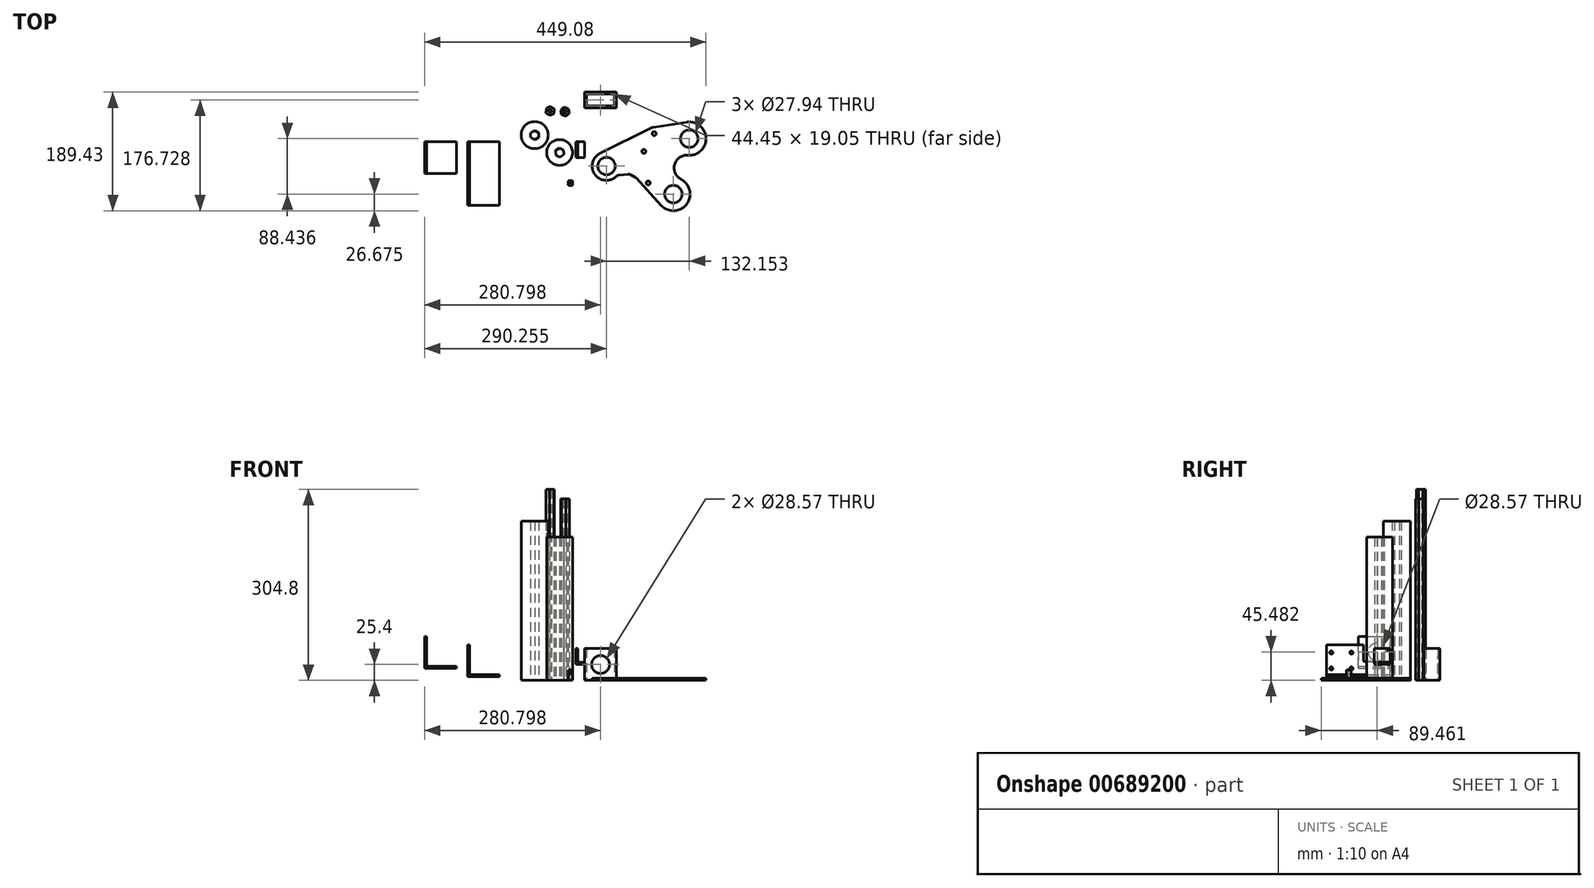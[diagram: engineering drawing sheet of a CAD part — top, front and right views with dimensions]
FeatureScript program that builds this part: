
annotation { "Feature Type Name" : "Feature", "Feature Type Description" : "" }
export const myFeature = defineFeature(function(context is Context, id is Id, definition is map)
    precondition{}
    {
        {
            var Q0;
            Q0=qCreatedBy(makeId("Top.planeOp"),FACE);
            var sketch = newSketch(context, id + "F0", { "sketchPlane" : qUnion([Q0])});
            skCircle(sketch, "E0", {"center": v(-44.27, 47.98) * mm, "radius": 2.55 * mm});
            skCircle(sketch, "E1.cCircle", {"center": v(-44.27, 47.98) * mm, "radius": 6.35 * mm, "construction": true});
            skLineSegment(sketch, "E1.0", {"start": v(-42.75, 40.8) * mm, "end": v(-49.72, 43.08) * mm});
            skLineSegment(sketch, "E1.1", {"start": v(-49.72, 43.08) * mm, "end": v(-51.24, 50.25) * mm});
            skLineSegment(sketch, "E1.2", {"start": v(-51.24, 50.25) * mm, "end": v(-45.79, 55.15) * mm});
            skLineSegment(sketch, "E1.3", {"start": v(-45.79, 55.15) * mm, "end": v(-38.82, 52.88) * mm});
            skLineSegment(sketch, "E1.4", {"start": v(-38.82, 52.88) * mm, "end": v(-37.3, 45.71) * mm});
            skLineSegment(sketch, "E1.5", {"start": v(-37.3, 45.71) * mm, "end": v(-42.75, 40.8) * mm});
            skPoint(sketch, "E1.0.midPoint", {"position": v(-46.23, 41.94) * mm});
            skCircle(sketch, "E2", {"center": v(-68.05, 49.07) * mm, "radius": 2.55 * mm});
            skCircle(sketch, "E3.cCircle", {"center": v(-68.05, 49.07) * mm, "radius": 6.35 * mm, "construction": true});
            skLineSegment(sketch, "E3.0", {"start": v(-62.1, 44.78) * mm, "end": v(-68.8, 41.78) * mm});
            skLineSegment(sketch, "E3.1", {"start": v(-68.8, 41.78) * mm, "end": v(-74.74, 46.07) * mm});
            skLineSegment(sketch, "E3.2", {"start": v(-74.74, 46.07) * mm, "end": v(-74, 53.36) * mm});
            skLineSegment(sketch, "E3.3", {"start": v(-74, 53.36) * mm, "end": v(-67.31, 56.37) * mm});
            skLineSegment(sketch, "E3.4", {"start": v(-67.31, 56.37) * mm, "end": v(-61.36, 52.08) * mm});
            skLineSegment(sketch, "E3.5", {"start": v(-61.36, 52.08) * mm, "end": v(-62.1, 44.78) * mm});
            skPoint(sketch, "E3.0.midPoint", {"position": v(-65.45, 43.28) * mm});
            skSolve(sketch);
        }
        {
            var Q0;
            Q0=makeQuery(id+"F0.imprint","IMPRINT",FACE,{"disambiguationData":[TD([[makeQuery(id+"F0.imprint","IMPRINT",EDGE,{"derivedFrom":sQuery(id+"F0.wireOp",EDGE,"E0")}),-1.0]])]});
            extrude(context, id + "F1", {"entities" : qUnion([Q0]), "depth" : 289.56 * mm, "offsetDistance" : 25.4 * mm});
        }
        {
            var Q0;
            Q0=makeQuery(id+"F0.imprint","IMPRINT",FACE,{"disambiguationData":[TD([[makeQuery(id+"F0.imprint","IMPRINT",EDGE,{"derivedFrom":sQuery(id+"F0.wireOp",EDGE,"E2")}),-1.0]])]});
            extrude(context, id + "F2", {"entities" : qUnion([Q0]), "depth" : 304.8 * mm, "offsetDistance" : 25.4 * mm});
        }
        {
            var Q0;
            Q0=qCreatedBy(makeId("Top.planeOp"),FACE);
            var sketch = newSketch(context, id + "F3", { "sketchPlane" : qUnion([Q0])});
            skCircle(sketch, "E4", {"center": v(128.7, -83.53) * mm, "radius": 13.97 * mm});
            skArc(sketch, "E5", {"start": v(150.08, -21.45) * mm, "mid": v(130.5, -37.06) * mm, "end": v(140.94, -59.83) * mm});
            skCircle(sketch, "E6", {"center": v(154.1, 4.91) * mm, "radius": 13.97 * mm});
            skCircle(sketch, "E7", {"center": v(154.1, 4.91) * mm, "radius": 20.64 * mm, "construction": true});
            skCircle(sketch, "E8", {"center": v(128.7, -83.53) * mm, "radius": 21.59 * mm, "construction": true});
            skArc(sketch, "E9", {"start": v(108.94, -101.43) * mm, "mid": v(132.45, -109.93) * mm, "end": v(152.67, -95.23) * mm});
            skLineSegment(sketch, "E10", {"start": v(150.12, 31.28) * mm, "end": v(96.62, 23.19) * mm});
            skLineSegment(sketch, "E11.bottom", {"start": v(224.17, -25.6) * mm, "end": v(499.33, -74.11) * mm, "construction": true});
            skLineSegment(sketch, "E11.top", {"start": v(215.35, -75.62) * mm, "end": v(490.5, -124.14) * mm, "construction": true});
            skLineSegment(sketch, "E11.left", {"start": v(224.17, -25.6) * mm, "end": v(215.35, -75.62) * mm, "construction": true});
            skLineSegment(sketch, "E11.right", {"start": v(499.33, -74.11) * mm, "end": v(490.5, -124.14) * mm, "construction": true});
            skPoint(sketch, "E11.middle", {"position": v(357.34, -74.87) * mm});
            skCircle(sketch, "E12", {"center": v(81.54, -15.44) * mm, "radius": 3.18 * mm});
            skCircle(sketch, "E13", {"center": v(81.54, -15.44) * mm, "radius": 6.87 * mm, "construction": true});
            skArc(sketch, "E14", {"start": v(11.8, -18.31) * mm, "mid": v(4, -52.95) * mm, "end": v(39.5, -53.45) * mm});
            skCircle(sketch, "E15", {"center": v(21.96, -38.8) * mm, "radius": 13.97 * mm});
            skArc(sketch, "E16.trimOffspring", {"start": v(152.67, -95.23) * mm, "mid": v(154.03, -75.14) * mm, "end": v(140.94, -59.83) * mm});
            skLineSegment(sketch, "E17", {"start": v(58.9, -51.49) * mm, "end": v(69.35, -57.7) * mm});
            skLineSegment(sketch, "E18", {"start": v(39.5, -53.45) * mm, "end": v(58.9, -51.49) * mm});
            skCircle(sketch, "E19", {"center": v(98.16, 13.02) * mm, "radius": 3.18 * mm});
            skCircle(sketch, "E20", {"center": v(98.16, 13.02) * mm, "radius": 6.87 * mm, "construction": true});
            skLineSegment(sketch, "E21", {"start": v(154.1, 4.91) * mm, "end": v(21.96, -38.8) * mm, "construction": true});
            skArc(sketch, "E22", {"start": v(96.62, 23.19) * mm, "mid": v(95.07, 22.83) * mm, "end": v(93.59, 22.23) * mm});
            skArc(sketch, "E23.trimOffspring", {"start": v(150.08, -21.45) * mm, "mid": v(180.78, 4.9) * mm, "end": v(150.12, 31.28) * mm});
            skLineSegment(sketch, "E24", {"start": v(69.35, -57.7) * mm, "end": v(108.94, -101.43) * mm});
            skArc(sketch, "E25.0.startCap", {"start": v(148.5, 21.86) * mm, "mid": v(171.06, 10.52) * mm, "end": v(159.71, -12.04) * mm, "construction": true});
            skArc(sketch, "E25.0.endCap", {"start": v(27.56, -55.75) * mm, "mid": v(5, -44.4) * mm, "end": v(16.35, -21.84) * mm, "construction": true});
            skLineSegment(sketch, "E25.0.left", {"start": v(159.71, -12.04) * mm, "end": v(27.56, -55.75) * mm, "construction": true});
            skLineSegment(sketch, "E25.0.right", {"start": v(148.5, 21.86) * mm, "end": v(16.35, -21.84) * mm, "construction": true});
            skCircle(sketch, "E26", {"center": v(88.6, -65.7) * mm, "radius": 3.18 * mm});
            skCircle(sketch, "E27", {"center": v(88.6, -65.7) * mm, "radius": 6.87 * mm, "construction": true});
            skLineSegment(sketch, "E28", {"start": v(81.54, -15.44) * mm, "end": v(88.5, -65) * mm, "construction": true});
            skLineSegment(sketch, "E29", {"start": v(93.59, 22.23) * mm, "end": v(11.8, -18.31) * mm});
            skSolve(sketch);
        }
        {
            var Q0;
            Q0=makeQuery(id+"F3.imprint","IMPRINT",FACE,{"disambiguationData":[TD([[makeQuery(id+"F3.imprint","IMPRINT",EDGE,{"derivedFrom":sQuery(id+"F3.wireOp",EDGE,"E4")}),-1.0]])]});
            var Q1;
            Q1=makeQuery(id+"F3.imprint","IMPRINT",FACE,{"disambiguationData":[TD([[makeQuery(id+"F3.imprint","IMPRINT",EDGE,{"derivedFrom":sQuery(id+"F3.wireOp",EDGE,"E15")}),-1.0]])]});
            var Q2;
            Q2=makeQuery(id+"F3.imprint","IMPRINT",FACE,{"disambiguationData":[TD([[makeQuery(id+"F3.imprint","IMPRINT",EDGE,{"derivedFrom":sQuery(id+"F3.wireOp",EDGE,"E6")}),-1.0]])]});
            var Q3;
            Q3=makeQuery(id+"F3.imprint","IMPRINT",FACE,{"disambiguationData":[TD([[makeQuery(id+"F3.imprint","IMPRINT",EDGE,{"derivedFrom":sQuery(id+"F3.wireOp",EDGE,"E19")}),-1.0]])]});
            extrude(context, id + "F4", {"entities" : qUnion([Q0, Q1, Q2, Q3]), "depth" : 3.17 * mm, "offsetDistance" : 25.4 * mm});
        }
        {
            var Q0;
            Q0=qCreatedBy(makeId("Top.planeOp"),FACE);
            var sketch = newSketch(context, id + "F5", { "sketchPlane" : qUnion([Q0])});
            skCircle(sketch, "E30", {"center": v(-92.7, 10.62) * mm, "radius": 21.59 * mm});
            skCircle(sketch, "E31.cCircle", {"center": v(-92.7, 10.62) * mm, "radius": 6.35 * mm, "construction": true});
            skLineSegment(sketch, "E31.0", {"start": v(-86.35, 6.96) * mm, "end": v(-92.7, 3.29) * mm});
            skLineSegment(sketch, "E31.1", {"start": v(-92.7, 3.29) * mm, "end": v(-99.05, 6.95) * mm});
            skLineSegment(sketch, "E31.2", {"start": v(-99.05, 6.95) * mm, "end": v(-99.06, 14.28) * mm});
            skLineSegment(sketch, "E31.3", {"start": v(-99.06, 14.28) * mm, "end": v(-92.7, 17.95) * mm});
            skLineSegment(sketch, "E31.4", {"start": v(-92.7, 17.95) * mm, "end": v(-86.36, 14.29) * mm});
            skLineSegment(sketch, "E31.5", {"start": v(-86.36, 14.29) * mm, "end": v(-86.35, 6.96) * mm});
            skPoint(sketch, "E31.0.midPoint", {"position": v(-89.53, 5.12) * mm});
            skSolve(sketch);
        }
        {
            var Q0;
            Q0=qSketchRegion(id+"F5",true);
            extrude(context, id + "F6", {"entities" : qUnion([Q0]), "depth" : 254 * mm, "offsetDistance" : 25.4 * mm});
        }
        {
            var Q0;
            Q0=qCreatedBy(makeId("Top.planeOp"),FACE);
            var sketch = newSketch(context, id + "F7", { "sketchPlane" : qUnion([Q0])});
            skCircle(sketch, "E32", {"center": v(-52.83, -17.18) * mm, "radius": 20.64 * mm});
            skCircle(sketch, "E33.cCircle", {"center": v(-52.83, -17.18) * mm, "radius": 6.35 * mm, "construction": true});
            skLineSegment(sketch, "E33.0", {"start": v(-46.29, -20.49) * mm, "end": v(-52.42, -24.5) * mm});
            skLineSegment(sketch, "E33.1", {"start": v(-52.42, -24.5) * mm, "end": v(-58.97, -21.2) * mm});
            skLineSegment(sketch, "E33.2", {"start": v(-58.97, -21.2) * mm, "end": v(-59.38, -13.88) * mm});
            skLineSegment(sketch, "E33.3", {"start": v(-59.38, -13.88) * mm, "end": v(-53.25, -9.86) * mm});
            skLineSegment(sketch, "E33.4", {"start": v(-53.25, -9.86) * mm, "end": v(-46.7, -13.17) * mm});
            skLineSegment(sketch, "E33.5", {"start": v(-46.7, -13.17) * mm, "end": v(-46.29, -20.49) * mm});
            skPoint(sketch, "E33.0.midPoint", {"position": v(-49.35, -22.5) * mm});
            skSolve(sketch);
        }
        {
            var Q0;
            Q0=makeQuery(id+"F7.imprint","IMPRINT",FACE,{"disambiguationData":[TD([[makeQuery(id+"F7.imprint","IMPRINT",EDGE,{"derivedFrom":sQuery(id+"F7.wireOp",EDGE,"E32")}),1.0]])]});
            extrude(context, id + "F8", {"entities" : qUnion([Q0]), "depth" : 228.6 * mm, "offsetDistance" : 25.4 * mm});
        }
        {
            var Q0;
            Q0=makeQuery(id+"F4.opExtrude","SWEPT_EDGE",EDGE,{"disambiguationData":[OSD([sQuery(id+"F3.wireOp",EDGE,"E10"),sQuery(id+"F3.wireOp",EDGE,"zxEpT3On-8kar-o6cf-8kjg-F8as8R4mIhED")])]});
            var Q1;
            Q1=makeQuery(id+"F4.opExtrude","SWEPT_EDGE",EDGE,{"disambiguationData":[OSD([sQuery(id+"F3.wireOp",EDGE,"E9"),sQuery(id+"F3.wireOp",EDGE,"c811799d-0cea-4770-864e-a57e5c831115.trimOffspring")])]});
            var Q2;
            Q2=makeQuery(id+"F4.opExtrude","SWEPT_EDGE",EDGE,{"disambiguationData":[OSD([sQuery(id+"F3.wireOp",EDGE,"4rDKKqdp-8bAY-1tYy-HnWQ-ftVNqJqIiV7y"),sQuery(id+"F3.wireOp",EDGE,"c811799d-0cea-4770-864e-a57e5c831115.trimOffspring")])]});
            var Q3;
            Q3=makeQuery(id+"F4.opExtrude","SWEPT_EDGE",EDGE,{"disambiguationData":[OSD([sQuery(id+"F3.wireOp",EDGE,"4rDKKqdp-8bAY-1tYy-HnWQ-ftVNqJqIiV7y"),sQuery(id+"F3.wireOp",EDGE,"E17")])]});
            var Q4;
            Q4=makeQuery(id+"F4.opExtrude","SWEPT_EDGE",EDGE,{"disambiguationData":[OSD([sQuery(id+"F3.wireOp",EDGE,"E14"),sQuery(id+"F3.wireOp",EDGE,"E18")])]});
            var Q5;
            Q5=makeQuery(id+"F4.opExtrude","SWEPT_EDGE",EDGE,{"disambiguationData":[OSD([sQuery(id+"F3.wireOp",EDGE,"E17"),sQuery(id+"F3.wireOp",EDGE,"E18")])]});
            var Q6;
            Q6=makeQuery(id+"F4.opExtrude","SWEPT_EDGE",EDGE,{"disambiguationData":[OSD([sQuery(id+"F3.wireOp",EDGE,"NqwyW4cG-bsPY-CdaV-dfMR-VU6UGlkVoTuP"),sQuery(id+"F3.wireOp",EDGE,"JTzklvK0-043S-AxbH-GuJj-bxXyPtfSXbyR")])]});
            fillet(context, id + "F9", {"entities" : qUnion([Q0, Q1, Q2, Q3, Q4, Q5, Q6]), "radius" : 6.35 * mm, "tangentPropagation" : true, "allowEdgeOverflow" : false});
        }
        {
            var Q0;
            Q0=qCreatedBy(makeId("Top.planeOp"),FACE);
            var sketch = newSketch(context, id + "F10", { "sketchPlane" : qUnion([Q0])});
            skLineSegment(sketch, "E34.bottom", {"start": v(37.9, 79.23) * mm, "end": v(-12.9, 79.23) * mm});
            skLineSegment(sketch, "E34.top", {"start": v(37.9, 53.83) * mm, "end": v(-12.9, 53.83) * mm});
            skLineSegment(sketch, "E34.left", {"start": v(37.9, 79.23) * mm, "end": v(37.9, 53.83) * mm});
            skLineSegment(sketch, "E34.right", {"start": v(-12.9, 79.23) * mm, "end": v(-12.9, 53.83) * mm});
            skPoint(sketch, "E34.middle", {"position": v(12.5, 66.53) * mm});
            skLineSegment(sketch, "E35.bottom", {"start": v(34.72, 76.05) * mm, "end": v(-9.73, 76.05) * mm});
            skLineSegment(sketch, "E35.top", {"start": v(34.72, 57) * mm, "end": v(-9.73, 57) * mm});
            skLineSegment(sketch, "E35.left", {"start": v(34.72, 76.05) * mm, "end": v(34.72, 57) * mm});
            skLineSegment(sketch, "E35.right", {"start": v(-9.73, 76.05) * mm, "end": v(-9.73, 57) * mm});
            skSolve(sketch);
        }
        {
            var Q0;
            Q0=makeQuery(id+"F10.imprint","IMPRINT",FACE,{"disambiguationData":[TD([[makeQuery(id+"F10.imprint","IMPRINT",EDGE,{"derivedFrom":sQuery(id+"F10.wireOp",EDGE,"E34.bottom")}),1.0]])]});
            extrude(context, id + "F11", {"entities" : qUnion([Q0]), "depth" : 50.8 * mm, "offsetDistance" : 25.4 * mm});
        }
        {
            var Q0;
            Q0=makeQuery(id+"F11.opExtrude","SWEPT_FACE",FACE,{"disambiguationData":[OSD([sQuery(id+"F10.wireOp",EDGE,"E34.bottom")])]});
            var sketch = newSketch(context, id + "F12", { "sketchPlane" : qUnion([Q0])});
            skLineSegment(sketch, "E36.0.0", {"start": v(-37.9, 0) * mm, "end": v(12.9, 0) * mm, "construction": true});
            skLineSegment(sketch, "E36.0.1", {"start": v(12.9, 0) * mm, "end": v(12.9, 50.8) * mm, "construction": true});
            skLineSegment(sketch, "E36.0.2", {"start": v(12.9, 50.8) * mm, "end": v(-37.9, 50.8) * mm, "construction": true});
            skLineSegment(sketch, "E36.0.3", {"start": v(-37.9, 50.8) * mm, "end": v(-37.9, 0) * mm, "construction": true});
            skCircle(sketch, "E37", {"center": v(-12.5, 25.4) * mm, "radius": 14.29 * mm});
            skPoint(sketch, "E37.centerSnap0", {"position": v(-12.5, 50.8) * mm});
            skSolve(sketch);
        }
        {
            var Q0;
            Q0=makeQuery(id+"F12.imprint","IMPRINT",FACE,{"disambiguationData":[TD([[makeQuery(id+"F12.imprint","IMPRINT",EDGE,{"derivedFrom":sQuery(id+"F12.wireOp",EDGE,"E37")}),1.0]])]});
            var Q1;
            Q1=makeQuery(id+"F11.opExtrude","SWEPT_FACE",FACE,{"disambiguationData":[OSD([sQuery(id+"F10.wireOp",EDGE,"E34.top")])]});
            extrude(context, id + "F13", {"entities" : qUnion([Q0]), "operationType" : NewBodyOperationType.REMOVE, "endBound" : BoundingType.UP_TO_SURFACE, "oppositeDirection" : true, "depth" : 25.4 * mm, "endBoundEntityFace" : qUnion([Q1]), "offsetDistance" : 25.4 * mm});
        }
        {
            var Q0;
            Q0=qCreatedBy(makeId("Front.planeOp"),FACE);
            var sketch = newSketch(context, id + "F14", { "sketchPlane" : qUnion([Q0])});
            skLineSegment(sketch, "E38", {"start": v(-199.8, 56.53) * mm, "end": v(-199.8, 5.73) * mm});
            skLineSegment(sketch, "E39", {"start": v(-199.8, 5.73) * mm, "end": v(-149, 5.73) * mm});
            skLineSegment(sketch, "E40", {"start": v(-149, 5.73) * mm, "end": v(-149, 8.9) * mm});
            skLineSegment(sketch, "E41", {"start": v(-149, 8.9) * mm, "end": v(-196.63, 8.9) * mm});
            skLineSegment(sketch, "E42", {"start": v(-196.63, 8.9) * mm, "end": v(-196.63, 56.53) * mm});
            skLineSegment(sketch, "E43", {"start": v(-196.63, 56.53) * mm, "end": v(-199.8, 56.53) * mm});
            skSolve(sketch);
        }
        {
            var Q0;
            Q0=qSketchRegion(id+"F14",true);
            extrude(context, id + "F15", {"entities" : qUnion([Q0]), "depth" : 101.6 * mm, "offsetDistance" : 25.4 * mm});
        }
        {
            var Q0;
            Q0=makeQuery(id+"F15.opExtrude","SWEPT_FACE",FACE,{"disambiguationData":[OSD([sQuery(id+"F14.wireOp",EDGE,"E42")])]});
            var sketch = newSketch(context, id + "F16", { "sketchPlane" : qUnion([Q0])});
            skLineSegment(sketch, "E44.0.0", {"start": v(0, 8.9) * mm, "end": v(0, 56.53) * mm, "construction": true});
            skLineSegment(sketch, "E44.0.1", {"start": v(0, 56.53) * mm, "end": v(-101.6, 56.53) * mm, "construction": true});
            skLineSegment(sketch, "E44.0.2", {"start": v(-101.6, 56.53) * mm, "end": v(-101.6, 8.9) * mm, "construction": true});
            skLineSegment(sketch, "E44.0.3", {"start": v(-101.6, 8.9) * mm, "end": v(0, 8.9) * mm, "construction": true});
            skLineSegment(sketch, "E45.bottom", {"start": v(-93.98, 44.46) * mm, "end": v(-61.85, 44.46) * mm, "construction": true});
            skLineSegment(sketch, "E45.top", {"start": v(-93.98, 19.06) * mm, "end": v(-61.85, 19.06) * mm, "construction": true});
            skLineSegment(sketch, "E45.left", {"start": v(-93.98, 44.46) * mm, "end": v(-93.98, 19.06) * mm, "construction": true});
            skLineSegment(sketch, "E45.right", {"start": v(-61.85, 44.46) * mm, "end": v(-61.85, 19.06) * mm, "construction": true});
            skPoint(sketch, "E45.middle", {"position": v(-77.91, 31.76) * mm});
            skCircle(sketch, "E46", {"center": v(-93.98, 44.46) * mm, "radius": 2.55 * mm});
            skCircle(sketch, "E47", {"center": v(-93.98, 19.06) * mm, "radius": 2.55 * mm});
            skCircle(sketch, "E48", {"center": v(-61.85, 19.06) * mm, "radius": 2.55 * mm});
            skCircle(sketch, "E49", {"center": v(-61.85, 44.46) * mm, "radius": 2.55 * mm});
            skLineSegment(sketch, "E50", {"start": v(-42.78, 56.53) * mm, "end": v(-42.78, 29.99) * mm});
            skLineSegment(sketch, "E51", {"start": v(-42.78, 29.99) * mm, "end": v(0, 29.99) * mm});
            skLineSegment(sketch, "E52", {"start": v(0, 29.99) * mm, "end": v(0, 56.53) * mm});
            skLineSegment(sketch, "E53", {"start": v(-42.78, 56.53) * mm, "end": v(0, 56.53) * mm});
            skSolve(sketch);
        }
        {
            var Q0;
            Q0=qSketchRegion(id+"F16",true);
            var Q1;
            Q1=makeQuery(id+"F15.opExtrude","SWEPT_FACE",FACE,{"disambiguationData":[OSD([sQuery(id+"F14.wireOp",EDGE,"E38")])]});
            extrude(context, id + "F17", {"entities" : qUnion([Q0]), "operationType" : NewBodyOperationType.REMOVE, "endBound" : BoundingType.UP_TO_SURFACE, "oppositeDirection" : true, "depth" : 25.4 * mm, "endBoundEntityFace" : qUnion([Q1]), "offsetDistance" : 25.4 * mm});
        }
        {
            var Q0;
            Q0=qCreatedBy(makeId("Front.planeOp"),FACE);
            var sketch = newSketch(context, id + "F18", { "sketchPlane" : qUnion([Q0])});
            skLineSegment(sketch, "E54", {"start": v(-26.85, 51.37) * mm, "end": v(-26.85, 25.97) * mm});
            skLineSegment(sketch, "E55", {"start": v(-26.85, 25.97) * mm, "end": v(-12.88, 25.97) * mm});
            skLineSegment(sketch, "E56", {"start": v(-12.88, 25.97) * mm, "end": v(-12.88, 29.14) * mm});
            skLineSegment(sketch, "E57", {"start": v(-12.88, 29.14) * mm, "end": v(-23.67, 29.14) * mm});
            skLineSegment(sketch, "E58", {"start": v(-23.67, 29.14) * mm, "end": v(-23.67, 51.37) * mm});
            skLineSegment(sketch, "E59", {"start": v(-23.67, 51.37) * mm, "end": v(-26.85, 51.37) * mm});
            skSolve(sketch);
        }
        {
            var Q0;
            Q0=makeQuery(id+"F18.imprint","IMPRINT",FACE,{"disambiguationData":[TD([[makeQuery(id+"F18.imprint","IMPRINT",EDGE,{"derivedFrom":sQuery(id+"F18.wireOp",EDGE,"E54")}),1.0]])]});
            extrude(context, id + "F19", {"entities" : qUnion([Q0]), "depth" : 25.4 * mm, "offsetDistance" : 25.4 * mm});
        }
        {
            var Q0;
            Q0=makeQuery(id+"F19.opExtrude","SWEPT_FACE",FACE,{"disambiguationData":[OSD([sQuery(id+"F18.wireOp",EDGE,"E58")])]});
            var sketch = newSketch(context, id + "F20", { "sketchPlane" : qUnion([Q0])});
            skLineSegment(sketch, "E60.0.0", {"start": v(0, 29.14) * mm, "end": v(0, 51.37) * mm, "construction": true});
            skLineSegment(sketch, "E60.0.1", {"start": v(0, 51.37) * mm, "end": v(-25.4, 51.37) * mm, "construction": true});
            skLineSegment(sketch, "E60.0.2", {"start": v(-25.4, 51.37) * mm, "end": v(-25.4, 29.14) * mm, "construction": true});
            skLineSegment(sketch, "E60.0.3", {"start": v(-25.4, 29.14) * mm, "end": v(0, 29.14) * mm, "construction": true});
            skCircle(sketch, "E61", {"center": v(-2.62, 48.83) * mm, "radius": 1.4 * mm});
            skPoint(sketch, "E61.centerSnap0", {"position": v(-12.7, 51.37) * mm});
            skLineSegment(sketch, "E62", {"start": v(-25.4, 29.14) * mm, "end": v(-25.4, 51.37) * mm});
            skLineSegment(sketch, "E63", {"start": v(0, 51.37) * mm, "end": v(0, 29.14) * mm});
            skLineSegment(sketch, "E64", {"start": v(-25.4, 51.37) * mm, "end": v(0, 51.37) * mm});
            skSolve(sketch);
        }
        {
            var Q0;
            {var subQ0=sQuery(id+"F20.wireOp",EDGE,"hmIuShvB-7MLo-ASm9-bvAH-xVIpYW9wqHkG");Q0=makeQuery(id+"F20.imprint","IMPRINT",FACE,{"disambiguationData":[TD([[makeQuery(id+"F20.imprint","IMPRINT",EDGE,{"derivedFrom":subQ0}),-1.0]])]});}
            var Q1;
            {var subQ0=sQuery(id+"F20.wireOp",EDGE,"VAUKN6EB-Ljji-Mb8e-VgR3-thsiO73GIbwf");Q1=makeQuery(id+"F20.imprint","IMPRINT",FACE,{"disambiguationData":[TD([[makeQuery(id+"F20.imprint","IMPRINT",EDGE,{"derivedFrom":subQ0}),1.0]])]});}
            var Q2;
            Q2=makeQuery(id+"F20.imprint","IMPRINT",FACE,{"disambiguationData":[TD([[makeQuery(id+"F20.imprint","IMPRINT",EDGE,{"derivedFrom":sQuery(id+"F20.wireOp",EDGE,"E61")}),1.0]])]});
            var Q3;
            Q3=makeQuery(id+"F19.opExtrude","SWEPT_FACE",FACE,{"disambiguationData":[OSD([sQuery(id+"F18.wireOp",EDGE,"E54")])]});
            extrude(context, id + "F21", {"entities" : qUnion([Q0, Q1, Q2]), "operationType" : NewBodyOperationType.REMOVE, "endBound" : BoundingType.UP_TO_SURFACE, "oppositeDirection" : true, "depth" : 25.4 * mm, "endBoundEntityFace" : qUnion([Q3]), "offsetDistance" : 25.4 * mm});
        }
        {
            var Q0;
            Q0=qCreatedBy(makeId("Top.planeOp"),FACE);
            var sketch = newSketch(context, id + "F22", { "sketchPlane" : qUnion([Q0])});
            skLineSegment(sketch, "E65.bottom", {"start": v(-32.18, -69.98) * mm, "end": v(-38.91, -69.98) * mm});
            skLineSegment(sketch, "E65.top", {"start": v(-32.18, -62.36) * mm, "end": v(-38.91, -62.36) * mm});
            skLineSegment(sketch, "E65.left", {"start": v(-32.18, -69.98) * mm, "end": v(-32.18, -62.36) * mm});
            skLineSegment(sketch, "E65.right", {"start": v(-38.91, -69.98) * mm, "end": v(-38.91, -62.36) * mm});
            skPoint(sketch, "E65.middle", {"position": v(-35.55, -66.17) * mm});
            skCircle(sketch, "E66", {"center": v(-35.55, -66.17) * mm, "radius": 1.78 * mm});
            skSolve(sketch);
        }
        {
            var Q0;
            Q0=makeQuery(id+"F22.imprint","IMPRINT",FACE,{"disambiguationData":[TD([[makeQuery(id+"F22.imprint","IMPRINT",EDGE,{"derivedFrom":sQuery(id+"F22.wireOp",EDGE,"E65.bottom")}),-1.0]])]});
            extrude(context, id + "F23", {"entities" : qUnion([Q0]), "depth" : 16.5 * mm, "offsetDistance" : 25.4 * mm});
        }
        {
            var Q0;
            Q0=makeQuery(id+"F23.opExtrude","SWEPT_FACE",FACE,{"disambiguationData":[OSD([sQuery(id+"F22.wireOp",EDGE,"E65.bottom")])]});
            var sketch = newSketch(context, id + "F24", { "sketchPlane" : qUnion([Q0])});
            skLineSegment(sketch, "E67.0.0", {"start": v(-38.91, 0) * mm, "end": v(-32.18, 0) * mm, "construction": true});
            skLineSegment(sketch, "E67.0.1", {"start": v(-32.18, 0) * mm, "end": v(-32.18, 16.51) * mm, "construction": true});
            skLineSegment(sketch, "E67.0.2", {"start": v(-32.18, 16.51) * mm, "end": v(-38.91, 16.51) * mm, "construction": true});
            skLineSegment(sketch, "E67.0.3", {"start": v(-38.91, 16.51) * mm, "end": v(-38.91, 0) * mm, "construction": true});
            skCircle(sketch, "E68", {"center": v(-35.55, 12.69) * mm, "radius": 2.55 * mm});
            skPoint(sketch, "E68.centerSnap0", {"position": v(-35.55, 16.51) * mm});
            skSolve(sketch);
        }
        {
            var Q0;
            Q0=makeQuery(id+"F24.imprint","IMPRINT",FACE,{"disambiguationData":[TD([[makeQuery(id+"F24.imprint","IMPRINT",EDGE,{"derivedFrom":sQuery(id+"F24.wireOp",EDGE,"E68")}),1.0]])]});
            var Q1;
            Q1=makeQuery(id+"F23.opExtrude","SWEPT_FACE",FACE,{"disambiguationData":[OSD([sQuery(id+"F22.wireOp",EDGE,"E65.top")])]});
            extrude(context, id + "F25", {"entities" : qUnion([Q0]), "operationType" : NewBodyOperationType.REMOVE, "endBound" : BoundingType.UP_TO_SURFACE, "oppositeDirection" : true, "depth" : 25.4 * mm, "endBoundEntityFace" : qUnion([Q1]), "offsetDistance" : 25.4 * mm});
        }
        {
            var Q0;
            Q0=qCreatedBy(makeId("Front.planeOp"),FACE);
            var sketch = newSketch(context, id + "F26", { "sketchPlane" : qUnion([Q0])});
            skLineSegment(sketch, "E69", {"start": v(-268.3, 69.93) * mm, "end": v(-268.3, 19.13) * mm});
            skLineSegment(sketch, "E70", {"start": v(-268.3, 19.13) * mm, "end": v(-217.5, 19.13) * mm});
            skLineSegment(sketch, "E71", {"start": v(-217.5, 19.13) * mm, "end": v(-217.5, 22.3) * mm});
            skLineSegment(sketch, "E72", {"start": v(-217.5, 22.3) * mm, "end": v(-265.13, 22.3) * mm});
            skLineSegment(sketch, "E73", {"start": v(-265.13, 22.3) * mm, "end": v(-265.13, 69.93) * mm});
            skLineSegment(sketch, "E74", {"start": v(-265.13, 69.93) * mm, "end": v(-268.3, 69.93) * mm});
            skSolve(sketch);
        }
        {
            var Q0;
            Q0=makeQuery(id+"F26.imprint","IMPRINT",FACE,{"disambiguationData":[TD([[makeQuery(id+"F26.imprint","IMPRINT",EDGE,{"derivedFrom":sQuery(id+"F26.wireOp",EDGE,"E69")}),1.0]])]});
            extrude(context, id + "F27", {"entities" : qUnion([Q0]), "depth" : 50.8 * mm, "offsetDistance" : 25.4 * mm});
        }
        {
            var Q0;
            Q0=makeQuery(id+"F27.opExtrude","SWEPT_FACE",FACE,{"disambiguationData":[OSD([sQuery(id+"F26.wireOp",EDGE,"E69")])]});
            var sketch = newSketch(context, id + "F28", { "sketchPlane" : qUnion([Q0])});
            skLineSegment(sketch, "E75.0.0", {"start": v(0, 69.93) * mm, "end": v(0, 19.13) * mm, "construction": true});
            skLineSegment(sketch, "E75.0.1", {"start": v(0, 19.13) * mm, "end": v(50.8, 19.13) * mm, "construction": true});
            skLineSegment(sketch, "E75.0.2", {"start": v(50.8, 19.13) * mm, "end": v(50.8, 69.93) * mm, "construction": true});
            skLineSegment(sketch, "E75.0.3", {"start": v(50.8, 69.93) * mm, "end": v(0, 69.93) * mm, "construction": true});
            skLineSegment(sketch, "E76", {"start": v(0, 22.3) * mm, "end": v(50.8, 22.3) * mm, "construction": true});
            skCircle(sketch, "E77", {"center": v(20.74, 45.48) * mm, "radius": 14.29 * mm});
            skSolve(sketch);
        }
        {
            var Q0;
            Q0=makeQuery(id+"F28.imprint","IMPRINT",FACE,{"disambiguationData":[TD([[makeQuery(id+"F28.imprint","IMPRINT",EDGE,{"derivedFrom":sQuery(id+"F28.wireOp",EDGE,"E77")}),1.0]])]});
            extrude(context, id + "F29", {"entities" : qUnion([Q0]), "operationType" : NewBodyOperationType.REMOVE, "oppositeDirection" : true, "depth" : 25.4 * mm, "offsetDistance" : 25.4 * mm});
        }
    });
